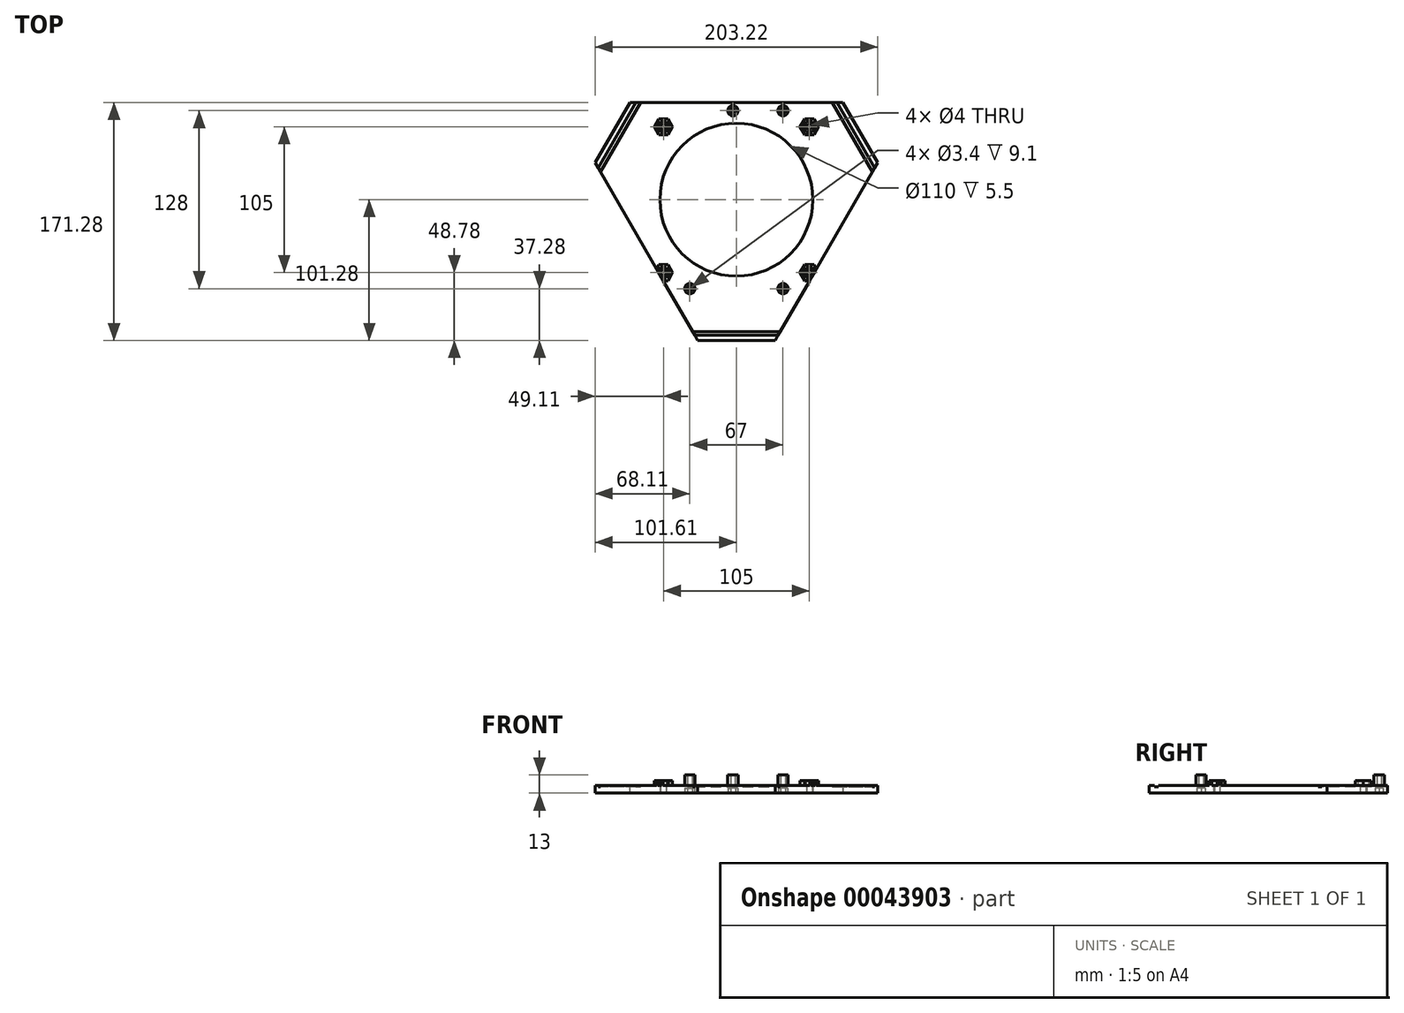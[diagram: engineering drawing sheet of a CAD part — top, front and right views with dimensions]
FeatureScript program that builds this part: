
annotation { "Feature Type Name" : "Feature", "Feature Type Description" : "" }
export const myFeature = defineFeature(function(context is Context, id is Id, definition is map)
    precondition{}
    {
        {
            var Q0;
            Q0=qCreatedBy(makeId("Top.planeOp"),FACE);
            var sketch = newSketch(context, id + "F0", { "sketchPlane" : qUnion([Q0])});
            skLineSegment(sketch, "E0", {"start": v(-136.39, -45.68) * mm, "end": v(-28.64, 140.95) * mm});
            skLineSegment(sketch, "E1", {"start": v(28.64, 140.95) * mm, "end": v(136.39, -45.68) * mm});
            skLineSegment(sketch, "E2", {"start": v(-107.75, -95.28) * mm, "end": v(107.75, -95.28) * mm});
            skLineSegment(sketch, "E3", {"start": v(0, 79.61) * mm, "end": v(0, -85.5) * mm, "construction": true});
            skLineSegment(sketch, "E4", {"start": v(-136.39, -45.68) * mm, "end": v(-107.75, -95.28) * mm});
            skLineSegment(sketch, "E5", {"start": v(107.75, -95.28) * mm, "end": v(136.39, -45.68) * mm});
            skLineSegment(sketch, "E6", {"start": v(-28.64, 140.95) * mm, "end": v(28.64, 140.95) * mm});
            skLineSegment(sketch, "E7", {"start": v(-28.64, 140.95) * mm, "end": v(-37.3, 145.95) * mm});
            skLineSegment(sketch, "E8", {"start": v(-37.3, 145.95) * mm, "end": v(-145.05, -40.68) * mm});
            skLineSegment(sketch, "E9", {"start": v(-145.05, -40.68) * mm, "end": v(-136.39, -45.68) * mm});
            skLineSegment(sketch, "E10", {"start": v(-107.75, -95.28) * mm, "end": v(-107.75, -105.28) * mm});
            skLineSegment(sketch, "E11", {"start": v(-107.75, -105.28) * mm, "end": v(107.75, -105.28) * mm});
            skLineSegment(sketch, "E12", {"start": v(107.75, -105.28) * mm, "end": v(107.75, -95.28) * mm});
            skLineSegment(sketch, "E13", {"start": v(136.39, -45.68) * mm, "end": v(145.05, -40.68) * mm});
            skLineSegment(sketch, "E14", {"start": v(145.05, -40.68) * mm, "end": v(37.3, 145.95) * mm});
            skLineSegment(sketch, "E15", {"start": v(37.3, 145.95) * mm, "end": v(28.64, 140.95) * mm});
            skPoint(sketch, "E16", {"position": v(0, -95.28) * mm});
            skLineSegment(sketch, "E17", {"start": v(-82.51, 47.64) * mm, "end": v(122.07, -70.48) * mm, "construction": true});
            skPoint(sketch, "E18", {"position": v(0, 0) * mm});
            skCircle(sketch, "E19", {"center": v(0, 0) * mm, "radius": 105.28 * mm});
            skLineSegment(sketch, "E20", {"start": v(-70.28, 136.45) * mm, "end": v(108.56, 136.45) * mm, "construction": true});
            skCircle(sketch, "E21", {"center": v(0, 0) * mm, "radius": 136.45 * mm, "construction": true});
            skCircle(sketch, "E22", {"center": v(0, 0) * mm, "radius": 132.5 * mm, "construction": true});
            skLineSegment(sketch, "E23.0", {"start": v(76.5, 132.5) * mm, "end": v(153, 0) * mm});
            skLineSegment(sketch, "E23.1", {"start": v(153, 0) * mm, "end": v(76.5, -132.5) * mm});
            skLineSegment(sketch, "E23.2", {"start": v(76.5, -132.5) * mm, "end": v(-76.5, -132.5) * mm});
            skLineSegment(sketch, "E23.3", {"start": v(-76.5, -132.5) * mm, "end": v(-153, 0) * mm});
            skLineSegment(sketch, "E23.4", {"start": v(-153, 0) * mm, "end": v(-76.5, 132.5) * mm});
            skLineSegment(sketch, "E23.5", {"start": v(-76.5, 132.5) * mm, "end": v(76.5, 132.5) * mm});
            skPoint(sketch, "E23.0.midPoint", {"position": v(114.75, 66.25) * mm});
            skLineSegment(sketch, "E24", {"start": v(-69.71, 166.45) * mm, "end": v(185.23, 166.45) * mm, "construction": true});
            skLineSegment(sketch, "E25", {"start": v(-113.33, 94.45) * mm, "end": v(229.2, 94.45) * mm, "construction": true});
            skCircle(sketch, "E26", {"center": v(0, 0) * mm, "radius": 94.45 * mm, "construction": true});
            skSolve(sketch);
        }
        {
            var Q0;
            {var subQ0=sQuery(id+"F0.wireOp",EDGE,"E19");var subQ6=sQuery(id+"F0.wireOp",EDGE,"E0");var subQ7=makeQuery(id+"F0.imprint","INTERSECT",VERTEX,{"disambiguationData":[OD(0.0)],"derivedFrom":[subQ6,subQ0]});Q0=makeQuery(id+"F0.imprint","IMPRINT",FACE,{"disambiguationData":[TD([[makeQuery(id+"F0.imprint","IMPRINT",EDGE,{"disambiguationData":[TD([[subQ7,-1.0]])],"derivedFrom":subQ6}),-1.0]])]});}
            var sketch = newSketch(context, id + "F1", { "sketchPlane" : qUnion([Q0])});
            skLineSegment(sketch, "E27", {"start": v(-101.61, 26.55) * mm, "end": v(-73.8, 74.72) * mm});
            skLineSegment(sketch, "E28", {"start": v(-73.8, 74.72) * mm, "end": v(73.8, 74.72) * mm});
            skLineSegment(sketch, "E29", {"start": v(73.8, 74.72) * mm, "end": v(101.61, 26.55) * mm});
            skLineSegment(sketch, "E30", {"start": v(101.61, 26.55) * mm, "end": v(27.81, -101.28) * mm});
            skLineSegment(sketch, "E31", {"start": v(27.81, -101.28) * mm, "end": v(-27.81, -101.28) * mm});
            skLineSegment(sketch, "E32", {"start": v(-27.81, -101.28) * mm, "end": v(-101.61, 26.55) * mm});
            skLineSegment(sketch, "E33", {"start": v(-66.3, 74.72) * mm, "end": v(-97.86, 20.05) * mm});
            skLineSegment(sketch, "E34", {"start": v(66.3, 74.72) * mm, "end": v(97.86, 20.05) * mm});
            skLineSegment(sketch, "E35", {"start": v(-31.56, -94.78) * mm, "end": v(31.56, -94.78) * mm});
            skLineSegment(sketch, "E36", {"start": v(-69.53, 74.72) * mm, "end": v(-99.48, 22.85) * mm});
            skLineSegment(sketch, "E37", {"start": v(69.53, 74.72) * mm, "end": v(99.48, 22.85) * mm});
            skLineSegment(sketch, "E38", {"start": v(-29.95, -97.58) * mm, "end": v(29.95, -97.58) * mm});
            skSolve(sketch);
        }
        {
            var Q0;
            {var subQ2=sQuery(id+"F1.wireOp",EDGE,"E33");Q0=makeQuery(id+"F1.imprint","IMPRINT",FACE,{"disambiguationData":[TD([[makeQuery(id+"F1.imprint","IMPRINT",EDGE,{"derivedFrom":subQ2}),1.0]])]});}
            var Q1;
            {var subQ2=sQuery(id+"F1.wireOp",EDGE,"E29");Q1=makeQuery(id+"F1.imprint","IMPRINT",FACE,{"disambiguationData":[TD([[makeQuery(id+"F1.imprint","IMPRINT",EDGE,{"derivedFrom":subQ2}),-1.0]])]});}
            var Q2;
            {var subQ2=sQuery(id+"F1.wireOp",EDGE,"E31");Q2=makeQuery(id+"F1.imprint","IMPRINT",FACE,{"disambiguationData":[TD([[makeQuery(id+"F1.imprint","IMPRINT",EDGE,{"derivedFrom":subQ2}),-1.0]])]});}
            var Q3;
            {var subQ2=sQuery(id+"F1.wireOp",EDGE,"E27");Q3=makeQuery(id+"F1.imprint","IMPRINT",FACE,{"disambiguationData":[TD([[makeQuery(id+"F1.imprint","IMPRINT",EDGE,{"derivedFrom":subQ2}),-1.0]])]});}
            extrude(context, id + "F2", {"entities" : qUnion([Q0, Q1, Q2, Q3]), "depth" : 5.5 * mm});
        }
        {
            var Q0;
            {var subQ7=sQuery(id+"F1.wireOp",EDGE,"E36");Q0=makeQuery(id+"F1.imprint","IMPRINT",FACE,{"disambiguationData":[TD([[makeQuery(id+"F1.imprint","IMPRINT",EDGE,{"derivedFrom":subQ7}),1.0]])]});}
            var Q1;
            {var subQ7=sQuery(id+"F1.wireOp",EDGE,"E38");Q1=makeQuery(id+"F1.imprint","IMPRINT",FACE,{"disambiguationData":[TD([[makeQuery(id+"F1.imprint","IMPRINT",EDGE,{"derivedFrom":subQ7}),1.0]])]});}
            var Q2;
            {var subQ7=sQuery(id+"F1.wireOp",EDGE,"E35");Q2=makeQuery(id+"F1.imprint","IMPRINT",FACE,{"disambiguationData":[TD([[makeQuery(id+"F1.imprint","IMPRINT",EDGE,{"derivedFrom":subQ7}),-1.0]])]});}
            var Q3;
            {var subQ7=sQuery(id+"F1.wireOp",EDGE,"E34");Q3=makeQuery(id+"F1.imprint","IMPRINT",FACE,{"disambiguationData":[TD([[makeQuery(id+"F1.imprint","IMPRINT",EDGE,{"derivedFrom":subQ7}),1.0]])]});}
            var Q4;
            {var subQ7=sQuery(id+"F1.wireOp",EDGE,"E37");Q4=makeQuery(id+"F1.imprint","IMPRINT",FACE,{"disambiguationData":[TD([[makeQuery(id+"F1.imprint","IMPRINT",EDGE,{"derivedFrom":subQ7}),-1.0]])]});}
            var Q5;
            {var subQ7=sQuery(id+"F1.wireOp",EDGE,"E33");Q5=makeQuery(id+"F1.imprint","IMPRINT",FACE,{"disambiguationData":[TD([[makeQuery(id+"F1.imprint","IMPRINT",EDGE,{"derivedFrom":subQ7}),-1.0]])]});}
            extrude(context, id + "F3", {"entities" : qUnion([Q0, Q1, Q2, Q3, Q4, Q5]), "operationType" : NewBodyOperationType.ADD, "depth" : 4.5 * mm});
        }
        {
            var Q0;
            Q0=makeQuery(id+"F2.opExtrude","CAP_FACE",FACE,{"disambiguationData":[OSD([sQuery(id+"F1.wireOp",EDGE,"E28"),sQuery(id+"F1.wireOp",EDGE,"E30"),sQuery(id+"F1.wireOp",EDGE,"E32"),sQuery(id+"F1.wireOp",EDGE,"E33"),sQuery(id+"F1.wireOp",EDGE,"E34"),sQuery(id+"F1.wireOp",EDGE,"E35")])],"isStart":false});
            var sketch = newSketch(context, id + "F4", { "sketchPlane" : qUnion([Q0])});
            skLineSegment(sketch, "E39.rect.bottom", {"start": v(33.5, -64) * mm, "end": v(-33.5, -64) * mm, "construction": true});
            skLineSegment(sketch, "E39.rect.top", {"start": v(33.5, 64) * mm, "end": v(-33.5, 64) * mm, "construction": true});
            skLineSegment(sketch, "E39.rect.left", {"start": v(33.5, -64) * mm, "end": v(33.5, 64) * mm, "construction": true});
            skLineSegment(sketch, "E39.rect.right", {"start": v(-33.5, -64) * mm, "end": v(-33.5, 64) * mm, "construction": true});
            skPoint(sketch, "E39.rect.middle", {"position": v(0, 0) * mm});
            skCircle(sketch, "E40", {"center": v(33.5, 64) * mm, "radius": 1.7 * mm});
            skCircle(sketch, "E41", {"center": v(33.5, -64) * mm, "radius": 1.7 * mm});
            skCircle(sketch, "E42", {"center": v(-33.5, -64) * mm, "radius": 1.7 * mm});
            skCircle(sketch, "E43", {"center": v(-2.5, 64) * mm, "radius": 1.7 * mm});
            skCircle(sketch, "E44", {"center": v(33.5, 64) * mm, "radius": 3.7 * mm});
            skCircle(sketch, "E45", {"center": v(-2.5, 64) * mm, "radius": 3.7 * mm});
            skCircle(sketch, "E46", {"center": v(33.5, -64) * mm, "radius": 3.7 * mm});
            skCircle(sketch, "E47", {"center": v(-33.5, -64) * mm, "radius": 3.7 * mm});
            skSolve(sketch);
        }
        {
            var Q0;
            Q0=makeQuery(id+"F4.imprint","IMPRINT",FACE,{"disambiguationData":[TD([[makeQuery(id+"F4.imprint","IMPRINT",EDGE,{"derivedFrom":sQuery(id+"F4.wireOp",EDGE,"E40")}),-1.0]])]});
            var Q1;
            Q1=makeQuery(id+"F4.imprint","IMPRINT",FACE,{"disambiguationData":[TD([[makeQuery(id+"F4.imprint","IMPRINT",EDGE,{"derivedFrom":sQuery(id+"F4.wireOp",EDGE,"E43")}),-1.0]])]});
            var Q2;
            Q2=makeQuery(id+"F4.imprint","IMPRINT",FACE,{"disambiguationData":[TD([[makeQuery(id+"F4.imprint","IMPRINT",EDGE,{"derivedFrom":sQuery(id+"F4.wireOp",EDGE,"E41")}),-1.0]])]});
            var Q3;
            Q3=makeQuery(id+"F4.imprint","IMPRINT",FACE,{"disambiguationData":[TD([[makeQuery(id+"F4.imprint","IMPRINT",EDGE,{"derivedFrom":sQuery(id+"F4.wireOp",EDGE,"E42")}),-1.0]])]});
            extrude(context, id + "F5", {"entities" : qUnion([Q0, Q1, Q2, Q3]), "operationType" : NewBodyOperationType.ADD, "depth" : 7.5 * mm});
        }
        {
            var Q0;
            Q0=makeQuery(id+"F5.boolean.opBoolean","SPLIT",FACE,{"disambiguationData":[TD([makeQuery(id+"F5.opExtrude","SWEPT_FACE",FACE,{"disambiguationData":[OSD([sQuery(id+"F4.wireOp",EDGE,"E42")])]})])],"derivedFrom":makeQuery(id+"F2.opExtrude","CAP_FACE",FACE,{"disambiguationData":[OSD([sQuery(id+"F1.wireOp",EDGE,"E28"),sQuery(id+"F1.wireOp",EDGE,"E30"),sQuery(id+"F1.wireOp",EDGE,"E32"),sQuery(id+"F1.wireOp",EDGE,"E33"),sQuery(id+"F1.wireOp",EDGE,"E34"),sQuery(id+"F1.wireOp",EDGE,"E35")])],"isStart":false})});
            var Q1;
            Q1=makeQuery(id+"F5.boolean.opBoolean","SPLIT",FACE,{"disambiguationData":[TD([makeQuery(id+"F5.opExtrude","SWEPT_FACE",FACE,{"disambiguationData":[OSD([sQuery(id+"F4.wireOp",EDGE,"E41")])]})])],"derivedFrom":makeQuery(id+"F2.opExtrude","CAP_FACE",FACE,{"disambiguationData":[OSD([sQuery(id+"F1.wireOp",EDGE,"E28"),sQuery(id+"F1.wireOp",EDGE,"E30"),sQuery(id+"F1.wireOp",EDGE,"E32"),sQuery(id+"F1.wireOp",EDGE,"E33"),sQuery(id+"F1.wireOp",EDGE,"E34"),sQuery(id+"F1.wireOp",EDGE,"E35")])],"isStart":false})});
            var Q2;
            Q2=makeQuery(id+"F5.boolean.opBoolean","SPLIT",FACE,{"disambiguationData":[TD([makeQuery(id+"F5.opExtrude","SWEPT_FACE",FACE,{"disambiguationData":[OSD([sQuery(id+"F4.wireOp",EDGE,"E43")])]})])],"derivedFrom":makeQuery(id+"F2.opExtrude","CAP_FACE",FACE,{"disambiguationData":[OSD([sQuery(id+"F1.wireOp",EDGE,"E28"),sQuery(id+"F1.wireOp",EDGE,"E30"),sQuery(id+"F1.wireOp",EDGE,"E32"),sQuery(id+"F1.wireOp",EDGE,"E33"),sQuery(id+"F1.wireOp",EDGE,"E34"),sQuery(id+"F1.wireOp",EDGE,"E35")])],"isStart":false})});
            var Q3;
            Q3=makeQuery(id+"F5.boolean.opBoolean","SPLIT",FACE,{"disambiguationData":[TD([makeQuery(id+"F5.opExtrude","SWEPT_FACE",FACE,{"disambiguationData":[OSD([sQuery(id+"F4.wireOp",EDGE,"E40")])]})])],"derivedFrom":makeQuery(id+"F2.opExtrude","CAP_FACE",FACE,{"disambiguationData":[OSD([sQuery(id+"F1.wireOp",EDGE,"E28"),sQuery(id+"F1.wireOp",EDGE,"E30"),sQuery(id+"F1.wireOp",EDGE,"E32"),sQuery(id+"F1.wireOp",EDGE,"E33"),sQuery(id+"F1.wireOp",EDGE,"E34"),sQuery(id+"F1.wireOp",EDGE,"E35")])],"isStart":false})});
            extrude(context, id + "F6", {"entities" : qUnion([Q0, Q1, Q2, Q3]), "operationType" : NewBodyOperationType.REMOVE, "oppositeDirection" : true, "depth" : 25 * mm});
        }
        {
            var Q0;
            {var subQ0=sQuery(id+"F0.wireOp",EDGE,"E19");var subQ6=sQuery(id+"F0.wireOp",EDGE,"E0");var subQ7=makeQuery(id+"F0.imprint","INTERSECT",VERTEX,{"disambiguationData":[OD(0.0)],"derivedFrom":[subQ6,subQ0]});Q0=makeQuery(id+"F0.imprint","IMPRINT",FACE,{"disambiguationData":[TD([[makeQuery(id+"F0.imprint","IMPRINT",EDGE,{"disambiguationData":[TD([[subQ7,-1.0]])],"derivedFrom":subQ6}),-1.0]])]});}
            var sketch = newSketch(context, id + "F7", { "sketchPlane" : qUnion([Q0])});
            skLineSegment(sketch, "E48.rect.bottom", {"start": v(52.5, 52.5) * mm, "end": v(-52.5, 52.5) * mm, "construction": true});
            skLineSegment(sketch, "E48.rect.top", {"start": v(52.5, -52.5) * mm, "end": v(-52.5, -52.5) * mm, "construction": true});
            skLineSegment(sketch, "E48.rect.left", {"start": v(52.5, 52.5) * mm, "end": v(52.5, -52.5) * mm, "construction": true});
            skLineSegment(sketch, "E48.rect.right", {"start": v(-52.5, 52.5) * mm, "end": v(-52.5, -52.5) * mm, "construction": true});
            skPoint(sketch, "E48.rect.middle", {"position": v(0, 0) * mm});
            skCircle(sketch, "E49", {"center": v(52.5, 52.5) * mm, "radius": 2 * mm});
            skCircle(sketch, "E50", {"center": v(52.5, -52.5) * mm, "radius": 2 * mm});
            skCircle(sketch, "E51", {"center": v(-52.5, -52.5) * mm, "radius": 2 * mm});
            skCircle(sketch, "E52", {"center": v(-52.5, 52.5) * mm, "radius": 2 * mm});
            skCircle(sketch, "E53", {"center": v(0, 0) * mm, "radius": 55 * mm});
            skCircle(sketch, "E54.cCircle", {"center": v(-33.5, -64) * mm, "radius": 3 * mm, "construction": true});
            skLineSegment(sketch, "E54.0", {"start": v(-30.04, -64) * mm, "end": v(-31.77, -67) * mm});
            skLineSegment(sketch, "E54.1", {"start": v(-31.77, -67) * mm, "end": v(-35.23, -67) * mm});
            skLineSegment(sketch, "E54.2", {"start": v(-35.23, -67) * mm, "end": v(-36.96, -64) * mm});
            skLineSegment(sketch, "E54.3", {"start": v(-36.96, -64) * mm, "end": v(-35.23, -61) * mm});
            skLineSegment(sketch, "E54.4", {"start": v(-35.23, -61) * mm, "end": v(-31.77, -61) * mm});
            skLineSegment(sketch, "E54.5", {"start": v(-31.77, -61) * mm, "end": v(-30.04, -64) * mm});
            skPoint(sketch, "E54.0.midPoint", {"position": v(-30.9, -65.5) * mm});
            skCircle(sketch, "E55.cCircle", {"center": v(33.5, -64) * mm, "radius": 3 * mm, "construction": true});
            skLineSegment(sketch, "E55.0", {"start": v(35.23, -67) * mm, "end": v(31.77, -67) * mm});
            skLineSegment(sketch, "E55.1", {"start": v(31.77, -67) * mm, "end": v(30.04, -64) * mm});
            skLineSegment(sketch, "E55.2", {"start": v(30.04, -64) * mm, "end": v(31.77, -61) * mm});
            skLineSegment(sketch, "E55.3", {"start": v(31.77, -61) * mm, "end": v(35.23, -61) * mm});
            skLineSegment(sketch, "E55.4", {"start": v(35.23, -61) * mm, "end": v(36.96, -64) * mm});
            skLineSegment(sketch, "E55.5", {"start": v(36.96, -64) * mm, "end": v(35.23, -67) * mm});
            skPoint(sketch, "E55.0.midPoint", {"position": v(33.5, -67) * mm});
            skCircle(sketch, "E56.cCircle", {"center": v(-2.5, 64) * mm, "radius": 3 * mm, "construction": true});
            skLineSegment(sketch, "E56.0", {"start": v(-0.77, 61) * mm, "end": v(-4.23, 61) * mm});
            skLineSegment(sketch, "E56.1", {"start": v(-4.23, 61) * mm, "end": v(-5.96, 64) * mm});
            skLineSegment(sketch, "E56.2", {"start": v(-5.96, 64) * mm, "end": v(-4.23, 67) * mm});
            skLineSegment(sketch, "E56.3", {"start": v(-4.23, 67) * mm, "end": v(-0.77, 67) * mm});
            skLineSegment(sketch, "E56.4", {"start": v(-0.77, 67) * mm, "end": v(0.96, 64) * mm});
            skLineSegment(sketch, "E56.5", {"start": v(0.96, 64) * mm, "end": v(-0.77, 61) * mm});
            skPoint(sketch, "E56.0.midPoint", {"position": v(-2.5, 61) * mm});
            skCircle(sketch, "E57.cCircle", {"center": v(33.5, 64) * mm, "radius": 3 * mm, "construction": true});
            skLineSegment(sketch, "E57.0", {"start": v(35.23, 61) * mm, "end": v(31.77, 61) * mm});
            skLineSegment(sketch, "E57.1", {"start": v(31.77, 61) * mm, "end": v(30.04, 64) * mm});
            skLineSegment(sketch, "E57.2", {"start": v(30.04, 64) * mm, "end": v(31.77, 67) * mm});
            skLineSegment(sketch, "E57.3", {"start": v(31.77, 67) * mm, "end": v(35.23, 67) * mm});
            skLineSegment(sketch, "E57.4", {"start": v(35.23, 67) * mm, "end": v(36.96, 64) * mm});
            skLineSegment(sketch, "E57.5", {"start": v(36.96, 64) * mm, "end": v(35.23, 61) * mm});
            skPoint(sketch, "E57.0.midPoint", {"position": v(33.5, 61) * mm});
            skSolve(sketch);
        }
        {
            var Q0;
            Q0=qSketchRegion(id+"F7",true);
            extrude(context, id + "F8", {"entities" : qUnion([Q0]), "operationType" : NewBodyOperationType.REMOVE, "depth" : 25 * mm});
        }
        {
            var Q0;
            Q0=qSketchRegion(id+"F4",true);
            var Q1;
            Q1=makeQuery(id+"F5.opExtrude","CAP_FACE",FACE,{"disambiguationData":[OSD([sQuery(id+"F4.wireOp",EDGE,"E40"),sQuery(id+"F4.wireOp",EDGE,"E44")])],"isStart":false});
            extrude(context, id + "F9", {"entities" : qUnion([Q0]), "operationType" : NewBodyOperationType.ADD, "endBound" : BoundingType.UP_TO_SURFACE, "endBoundEntityFace" : qUnion([Q1]), "depth" : 25 * mm, "hasSecondDirection" : true, "secondDirectionOppositeDirection" : true, "secondDirectionDepth" : 2 * mm});
        }
        {
            var Q0;
            Q0=makeQuery(id+"F4.imprint","IMPRINT",FACE,{"disambiguationData":[TD([[makeQuery(id+"F4.imprint","IMPRINT",EDGE,{"derivedFrom":sQuery(id+"F4.wireOp",EDGE,"E40")}),1.0]])]});
            var Q1;
            Q1=makeQuery(id+"F4.imprint","IMPRINT",FACE,{"disambiguationData":[TD([[makeQuery(id+"F4.imprint","IMPRINT",EDGE,{"derivedFrom":sQuery(id+"F4.wireOp",EDGE,"E43")}),1.0]])]});
            var Q2;
            Q2=makeQuery(id+"F4.imprint","IMPRINT",FACE,{"disambiguationData":[TD([[makeQuery(id+"F4.imprint","IMPRINT",EDGE,{"derivedFrom":sQuery(id+"F4.wireOp",EDGE,"E42")}),1.0]])]});
            var Q3;
            Q3=makeQuery(id+"F4.imprint","IMPRINT",FACE,{"disambiguationData":[TD([[makeQuery(id+"F4.imprint","IMPRINT",EDGE,{"derivedFrom":sQuery(id+"F4.wireOp",EDGE,"E41")}),1.0]])]});
            var Q4;
            Q4=makeQuery(id+"F9.opExtrude","CAP_FACE",FACE,{"disambiguationData":[OSD([sQuery(id+"F4.wireOp",EDGE,"E42"),sQuery(id+"F4.wireOp",EDGE,"E47")])],"isStart":true});
            extrude(context, id + "F10", {"entities" : qUnion([Q0, Q1, Q2, Q3]), "operationType" : NewBodyOperationType.ADD, "endBound" : BoundingType.UP_TO_SURFACE, "oppositeDirection" : true, "endBoundEntityFace" : qUnion([Q4]), "depth" : 0.4 * mm, "hasSecondDirection" : true, "secondDirectionOppositeDirection" : true, "secondDirectionDepth" : 1.6 * mm});
        }
        {
            var Q0;
            {var subQ0=sQuery(id+"F1.wireOp",EDGE,"E28");var subQ1=sQuery(id+"F1.wireOp",EDGE,"E30");var subQ2=sQuery(id+"F1.wireOp",EDGE,"E32");var subQ3=sQuery(id+"F1.wireOp",EDGE,"E33");var subQ4=sQuery(id+"F1.wireOp",EDGE,"E34");var subQ5=sQuery(id+"F1.wireOp",EDGE,"E35");Q0=makeQuery(id+"F5.boolean.opBoolean","SPLIT",FACE,{"disambiguationData":[TD([makeQuery(id+"F2.opExtrude","SWEPT_FACE",FACE,{"disambiguationData":[OSD([subQ3])]})])],"derivedFrom":makeQuery(id+"F2.opExtrude","CAP_FACE",FACE,{"disambiguationData":[OSD([subQ0,subQ1,subQ2,subQ3,subQ4,subQ5])],"isStart":false})});}
            var sketch = newSketch(context, id + "F11", { "sketchPlane" : qUnion([Q0])});
            skCircle(sketch, "E58.cCircle", {"center": v(-52.5, -52.5) * mm, "radius": 3.75 * mm, "construction": true});
            skLineSegment(sketch, "E58.0", {"start": v(-54.67, -48.75) * mm, "end": v(-50.33, -48.75) * mm});
            skLineSegment(sketch, "E58.1", {"start": v(-50.33, -48.75) * mm, "end": v(-48.17, -52.5) * mm});
            skLineSegment(sketch, "E58.2", {"start": v(-48.17, -52.5) * mm, "end": v(-50.33, -56.25) * mm});
            skLineSegment(sketch, "E58.3", {"start": v(-50.33, -56.25) * mm, "end": v(-54.67, -56.25) * mm});
            skLineSegment(sketch, "E58.4", {"start": v(-54.67, -56.25) * mm, "end": v(-56.83, -52.5) * mm});
            skLineSegment(sketch, "E58.5", {"start": v(-56.83, -52.5) * mm, "end": v(-54.67, -48.75) * mm});
            skPoint(sketch, "E58.0.midPoint", {"position": v(-52.5, -48.75) * mm});
            skCircle(sketch, "E59.cCircle", {"center": v(52.5, -52.5) * mm, "radius": 3.75 * mm, "construction": true});
            skLineSegment(sketch, "E59.0", {"start": v(50.33, -48.75) * mm, "end": v(54.67, -48.75) * mm});
            skLineSegment(sketch, "E59.1", {"start": v(54.67, -48.75) * mm, "end": v(56.83, -52.5) * mm});
            skLineSegment(sketch, "E59.2", {"start": v(56.83, -52.5) * mm, "end": v(54.67, -56.25) * mm});
            skLineSegment(sketch, "E59.3", {"start": v(54.67, -56.25) * mm, "end": v(50.33, -56.25) * mm});
            skLineSegment(sketch, "E59.4", {"start": v(50.33, -56.25) * mm, "end": v(48.17, -52.5) * mm});
            skLineSegment(sketch, "E59.5", {"start": v(48.17, -52.5) * mm, "end": v(50.33, -48.75) * mm});
            skPoint(sketch, "E59.0.midPoint", {"position": v(52.5, -48.75) * mm});
            skCircle(sketch, "E60.cCircle", {"center": v(-52.5, 52.5) * mm, "radius": 3.75 * mm, "construction": true});
            skLineSegment(sketch, "E60.0", {"start": v(-50.33, 48.75) * mm, "end": v(-54.67, 48.75) * mm});
            skLineSegment(sketch, "E60.1", {"start": v(-54.67, 48.75) * mm, "end": v(-56.83, 52.5) * mm});
            skLineSegment(sketch, "E60.2", {"start": v(-56.83, 52.5) * mm, "end": v(-54.67, 56.25) * mm});
            skLineSegment(sketch, "E60.3", {"start": v(-54.67, 56.25) * mm, "end": v(-50.33, 56.25) * mm});
            skLineSegment(sketch, "E60.4", {"start": v(-50.33, 56.25) * mm, "end": v(-48.17, 52.5) * mm});
            skLineSegment(sketch, "E60.5", {"start": v(-48.17, 52.5) * mm, "end": v(-50.33, 48.75) * mm});
            skPoint(sketch, "E60.0.midPoint", {"position": v(-52.5, 48.75) * mm});
            skCircle(sketch, "E61.cCircle", {"center": v(52.5, 52.5) * mm, "radius": 3.75 * mm, "construction": true});
            skLineSegment(sketch, "E61.0", {"start": v(54.67, 48.75) * mm, "end": v(50.33, 48.75) * mm});
            skLineSegment(sketch, "E61.1", {"start": v(50.33, 48.75) * mm, "end": v(48.17, 52.5) * mm});
            skLineSegment(sketch, "E61.2", {"start": v(48.17, 52.5) * mm, "end": v(50.33, 56.25) * mm});
            skLineSegment(sketch, "E61.3", {"start": v(50.33, 56.25) * mm, "end": v(54.67, 56.25) * mm});
            skLineSegment(sketch, "E61.4", {"start": v(54.67, 56.25) * mm, "end": v(56.83, 52.5) * mm});
            skLineSegment(sketch, "E61.5", {"start": v(56.83, 52.5) * mm, "end": v(54.67, 48.75) * mm});
            skPoint(sketch, "E61.0.midPoint", {"position": v(52.5, 48.75) * mm});
            skCircle(sketch, "E62.cCircle", {"center": v(-52.5, -52.5) * mm, "radius": 5.75 * mm, "construction": true});
            skLineSegment(sketch, "E62.0", {"start": v(-55.82, -46.75) * mm, "end": v(-49.18, -46.75) * mm});
            skLineSegment(sketch, "E62.1", {"start": v(-49.18, -46.75) * mm, "end": v(-45.86, -52.5) * mm});
            skLineSegment(sketch, "E62.2", {"start": v(-45.86, -52.5) * mm, "end": v(-49.18, -58.25) * mm});
            skLineSegment(sketch, "E62.3", {"start": v(-49.18, -58.25) * mm, "end": v(-55.82, -58.25) * mm});
            skLineSegment(sketch, "E62.4", {"start": v(-55.82, -58.25) * mm, "end": v(-59.14, -52.5) * mm});
            skLineSegment(sketch, "E62.5", {"start": v(-59.14, -52.5) * mm, "end": v(-55.82, -46.75) * mm});
            skPoint(sketch, "E62.0.midPoint", {"position": v(-52.5, -46.75) * mm});
            skCircle(sketch, "E63.cCircle", {"center": v(52.5, -52.5) * mm, "radius": 5.75 * mm, "construction": true});
            skLineSegment(sketch, "E63.0", {"start": v(49.18, -46.75) * mm, "end": v(55.82, -46.75) * mm});
            skLineSegment(sketch, "E63.1", {"start": v(55.82, -46.75) * mm, "end": v(59.14, -52.5) * mm});
            skLineSegment(sketch, "E63.2", {"start": v(59.14, -52.5) * mm, "end": v(55.82, -58.25) * mm});
            skLineSegment(sketch, "E63.3", {"start": v(55.82, -58.25) * mm, "end": v(49.18, -58.25) * mm});
            skLineSegment(sketch, "E63.4", {"start": v(49.18, -58.25) * mm, "end": v(45.86, -52.5) * mm});
            skLineSegment(sketch, "E63.5", {"start": v(45.86, -52.5) * mm, "end": v(49.18, -46.75) * mm});
            skPoint(sketch, "E63.0.midPoint", {"position": v(52.5, -46.75) * mm});
            skCircle(sketch, "E64.cCircle", {"center": v(-52.5, 52.5) * mm, "radius": 5.75 * mm, "construction": true});
            skLineSegment(sketch, "E64.0", {"start": v(-49.18, 46.75) * mm, "end": v(-55.82, 46.75) * mm});
            skLineSegment(sketch, "E64.1", {"start": v(-55.82, 46.75) * mm, "end": v(-59.14, 52.5) * mm});
            skLineSegment(sketch, "E64.2", {"start": v(-59.14, 52.5) * mm, "end": v(-55.82, 58.25) * mm});
            skLineSegment(sketch, "E64.3", {"start": v(-55.82, 58.25) * mm, "end": v(-49.18, 58.25) * mm});
            skLineSegment(sketch, "E64.4", {"start": v(-49.18, 58.25) * mm, "end": v(-45.86, 52.5) * mm});
            skLineSegment(sketch, "E64.5", {"start": v(-45.86, 52.5) * mm, "end": v(-49.18, 46.75) * mm});
            skPoint(sketch, "E64.0.midPoint", {"position": v(-52.5, 46.75) * mm});
            skCircle(sketch, "E65.cCircle", {"center": v(52.5, 52.5) * mm, "radius": 5.75 * mm, "construction": true});
            skLineSegment(sketch, "E65.0", {"start": v(55.82, 46.75) * mm, "end": v(49.18, 46.75) * mm});
            skLineSegment(sketch, "E65.1", {"start": v(49.18, 46.75) * mm, "end": v(45.86, 52.5) * mm});
            skLineSegment(sketch, "E65.2", {"start": v(45.86, 52.5) * mm, "end": v(49.18, 58.25) * mm});
            skLineSegment(sketch, "E65.3", {"start": v(49.18, 58.25) * mm, "end": v(55.82, 58.25) * mm});
            skLineSegment(sketch, "E65.4", {"start": v(55.82, 58.25) * mm, "end": v(59.14, 52.5) * mm});
            skLineSegment(sketch, "E65.5", {"start": v(59.14, 52.5) * mm, "end": v(55.82, 46.75) * mm});
            skPoint(sketch, "E65.0.midPoint", {"position": v(52.5, 46.75) * mm});
            skSolve(sketch);
        }
        {
            var Q0;
            Q0=makeQuery(id+"F11.imprint","IMPRINT",FACE,{"disambiguationData":[TD([[makeQuery(id+"F11.imprint","IMPRINT",EDGE,{"derivedFrom":sQuery(id+"F11.wireOp",EDGE,"E58.0")}),1.0]])]});
            var Q1;
            Q1=makeQuery(id+"F11.imprint","IMPRINT",FACE,{"disambiguationData":[TD([[makeQuery(id+"F11.imprint","IMPRINT",EDGE,{"derivedFrom":sQuery(id+"F11.wireOp",EDGE,"E59.0")}),1.0]])]});
            var Q2;
            Q2=makeQuery(id+"F11.imprint","IMPRINT",FACE,{"disambiguationData":[TD([[makeQuery(id+"F11.imprint","IMPRINT",EDGE,{"derivedFrom":sQuery(id+"F11.wireOp",EDGE,"E60.0")}),1.0]])]});
            var Q3;
            Q3=makeQuery(id+"F11.imprint","IMPRINT",FACE,{"disambiguationData":[TD([[makeQuery(id+"F11.imprint","IMPRINT",EDGE,{"derivedFrom":sQuery(id+"F11.wireOp",EDGE,"E61.0")}),1.0]])]});
            extrude(context, id + "F12", {"entities" : qUnion([Q0, Q1, Q2, Q3]), "operationType" : NewBodyOperationType.ADD, "depth" : 3.5 * mm});
        }
        {
            var Q0;
            Q0=qCreatedBy(makeId("Front.planeOp"),FACE);
            cPlane(context, id + "F13", {"entities" : qUnion([Q0]), "cplaneType" : CPlaneType.OFFSET, "offset" : 70 * mm, "oppositeDirection" : true, "width" : 150 * mm, "height" : 150 * mm});
        }
        {
            var Q0;
            Q0=qCreatedBy(id+"F13.planeOp",FACE);
            var sketch = newSketch(context, id + "F14", { "sketchPlane" : qUnion([Q0])});
            skLineSegment(sketch, "E66.bottom", {"start": v(-120.83, 93.34) * mm, "end": v(130.13, 93.34) * mm});
            skLineSegment(sketch, "E66.top", {"start": v(-120.83, -41.2) * mm, "end": v(130.13, -41.2) * mm});
            skLineSegment(sketch, "E66.left", {"start": v(-120.83, 93.34) * mm, "end": v(-120.83, -41.2) * mm});
            skLineSegment(sketch, "E66.right", {"start": v(130.13, 93.34) * mm, "end": v(130.13, -41.2) * mm});
            skSolve(sketch);
        }
        {
            var Q0;
            Q0=makeQuery(id+"F14.imprint","IMPRINT",FACE,{"disambiguationData":[TD([[makeQuery(id+"F14.imprint","IMPRINT",EDGE,{"derivedFrom":sQuery(id+"F14.wireOp",EDGE,"E66.bottom")}),-1.0]])]});
            extrude(context, id + "F15", {"entities" : qUnion([Q0]), "operationType" : NewBodyOperationType.REMOVE, "oppositeDirection" : true, "depth" : 25 * mm});
        }
    });
